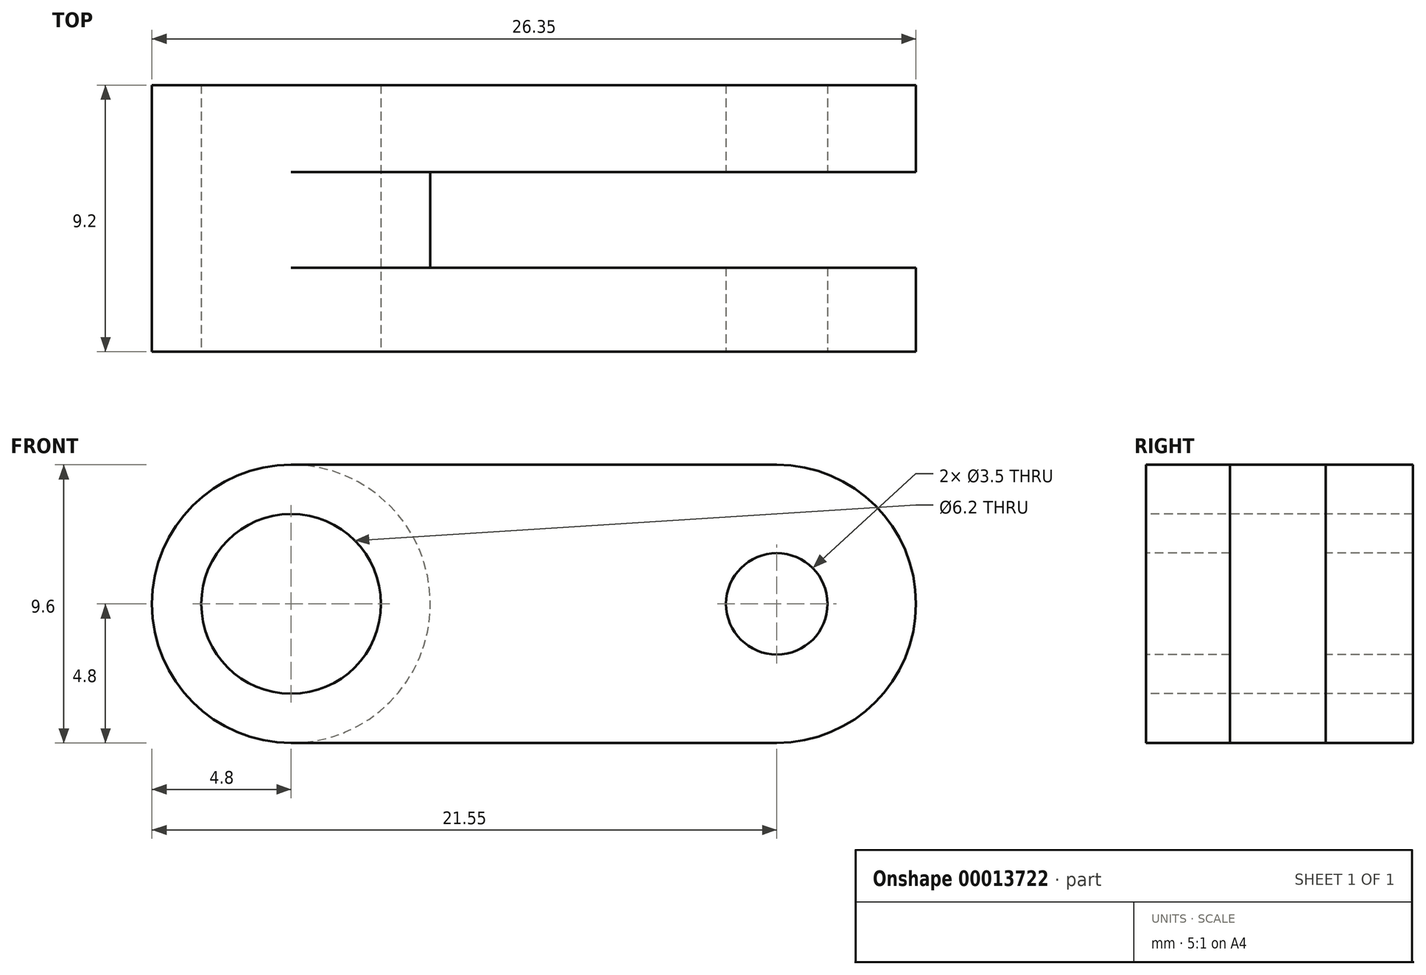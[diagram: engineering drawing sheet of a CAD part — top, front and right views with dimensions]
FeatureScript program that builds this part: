
annotation { "Feature Type Name" : "Feature", "Feature Type Description" : "" }
export const myFeature = defineFeature(function(context is Context, id is Id, definition is map)
    precondition{}
    {
        {
            var Q0;
            Q0=qCreatedBy(makeId("Front.planeOp"),FACE);
            var sketch = newSketch(context, id + "F0", { "sketchPlane" : qUnion([Q0])});
            skCircle(sketch, "E0", {"center": v(0, 0) * mm, "radius": 5 * mm, "construction": true});
            skCircle(sketch, "E1", {"center": v(0, -16.75) * mm, "radius": 1.75 * mm});
            skLineSegment(sketch, "E2", {"start": v(0, -15) * mm, "end": v(0, -5) * mm, "construction": true});
            skPoint(sketch, "E3.orphan", {"position": v(0, 5) * mm});
            skLineSegment(sketch, "E4", {"start": v(-8, 5) * mm, "end": v(-9, -16.75) * mm, "construction": true});
            skLineSegment(sketch, "E5", {"start": v(8, 5) * mm, "end": v(9, -16.75) * mm, "construction": true});
            skLineSegment(sketch, "E6", {"start": v(0, 5) * mm, "end": v(-8, 5) * mm, "construction": true});
            skLineSegment(sketch, "E7", {"start": v(0, 5) * mm, "end": v(8, 5) * mm, "construction": true});
            skLineSegment(sketch, "E8", {"start": v(0, -16.75) * mm, "end": v(9, -16.75) * mm, "construction": true});
            skLineSegment(sketch, "E9", {"start": v(0, -16.75) * mm, "end": v(-9, -16.75) * mm, "construction": true});
            skLineSegment(sketch, "E10", {"start": v(-5, 0) * mm, "end": v(-5, 5) * mm, "construction": true});
            skLineSegment(sketch, "E11", {"start": v(5, 0) * mm, "end": v(5, 5) * mm, "construction": true});
            skCircle(sketch, "E12", {"center": v(0, 0) * mm, "radius": 3.1 * mm});
            skCircle(sketch, "E13", {"center": v(0, 0) * mm, "radius": 4.8 * mm});
            skArc(sketch, "E14", {"start": v(-4.8, -16.75) * mm, "mid": v(0, -21.55) * mm, "end": v(4.8, -16.75) * mm});
            skLineSegment(sketch, "E15", {"start": v(-4.8, 0) * mm, "end": v(-4.8, -16.75) * mm});
            skLineSegment(sketch, "E16", {"start": v(4.8, 0) * mm, "end": v(4.8, -16.75) * mm});
            skSolve(sketch);
        }
        {
            var Q0;
            Q0=makeQuery(id+"F0.imprint","IMPRINT",FACE,{"disambiguationData":[TD([[makeQuery(id+"F0.imprint","IMPRINT",EDGE,{"derivedFrom":sQuery(id+"F0.wireOp",EDGE,"E12")}),-1.0]])]});
            var Q1;
            Q1=makeQuery(id+"F0.imprint","IMPRINT",FACE,{"disambiguationData":[TD([[makeQuery(id+"F0.imprint","IMPRINT",EDGE,{"derivedFrom":sQuery(id+"F0.wireOp",EDGE,"E1")}),-1.0]])]});
            extrude(context, id + "F1", {"entities" : qUnion([Q0, Q1]), "oppositeDirection" : true, "depth" : 3 * mm});
        }
        {
            var Q0;
            Q0=makeQuery(id+"F0.imprint","IMPRINT",FACE,{"disambiguationData":[TD([[makeQuery(id+"F0.imprint","IMPRINT",EDGE,{"derivedFrom":sQuery(id+"F0.wireOp",EDGE,"E1")}),-1.0]])]});
            var Q1;
            Q1=makeQuery(id+"F0.imprint","IMPRINT",FACE,{"disambiguationData":[TD([[makeQuery(id+"F0.imprint","IMPRINT",EDGE,{"derivedFrom":sQuery(id+"F0.wireOp",EDGE,"E12")}),-1.0]])]});
            extrude(context, id + "F2", {"entities" : qUnion([Q0, Q1]), "operationType" : NewBodyOperationType.ADD, "depth" : (3.2 + 3) * mm});
        }
        {
            var Q0;
            Q0=makeQuery(id+"F0.imprint","IMPRINT",FACE,{"disambiguationData":[TD([[makeQuery(id+"F0.imprint","IMPRINT",EDGE,{"derivedFrom":sQuery(id+"F0.wireOp",EDGE,"E1")}),-1.0]])]});
            var Q1;
            Q1=makeQuery(id+"F0.imprint","IMPRINT",FACE,{"disambiguationData":[TD([[makeQuery(id+"F0.imprint","IMPRINT",EDGE,{"derivedFrom":sQuery(id+"F0.wireOp",EDGE,"E12")}),-1.0]])]});
            extrude(context, id + "F3", {"entities" : qUnion([Q0, Q1]), "operationType" : NewBodyOperationType.REMOVE, "depth" : 3.3 * mm});
        }
        {
            var Q0;
            Q0=makeQuery(id+"F0.imprint","IMPRINT",FACE,{"disambiguationData":[TD([[makeQuery(id+"F0.imprint","IMPRINT",EDGE,{"derivedFrom":sQuery(id+"F0.wireOp",EDGE,"E12")}),-1.0]])]});
            extrude(context, id + "F4", {"entities" : qUnion([Q0]), "operationType" : NewBodyOperationType.ADD, "endBound" : BoundingType.UP_TO_NEXT, "depth" : 3.76 * mm});
        }
        {
            var Q0;
            Q0=makeQuery(id+"F3.boolean.opBoolean","SPLIT",BODY,{"disambiguationData":[OD(0.0)],"derivedFrom":makeQuery(id+"F1.opExtrude","SWEPT_BODY",BODY,{"disambiguationData":[OSD([sQuery(id+"F0.wireOp",EDGE,"E1"),sQuery(id+"F0.wireOp",EDGE,"E12"),sQuery(id+"F0.wireOp",EDGE,"E13"),sQuery(id+"F0.wireOp",EDGE,"E14"),sQuery(id+"F0.wireOp",EDGE,"E15"),sQuery(id+"F0.wireOp",EDGE,"E16")])]})});
            var Q1;
            Q1=makeQuery(id+"F2.opExtrude","CAP_EDGE",EDGE,{"disambiguationData":[OSD([sQuery(id+"F0.wireOp",EDGE,"E12")])],"isStart":false});
            transform(context, id + "F5", {"entities" : qUnion([Q0]), "transformType" : TransformType.ROTATION, "transformAxis" : qUnion([Q1]), "angle" : 90 * degree, "oppositeX" : false, "oppositeY" : false, "oppositeZ" : false, "makeCopy" : false});
        }
    });
